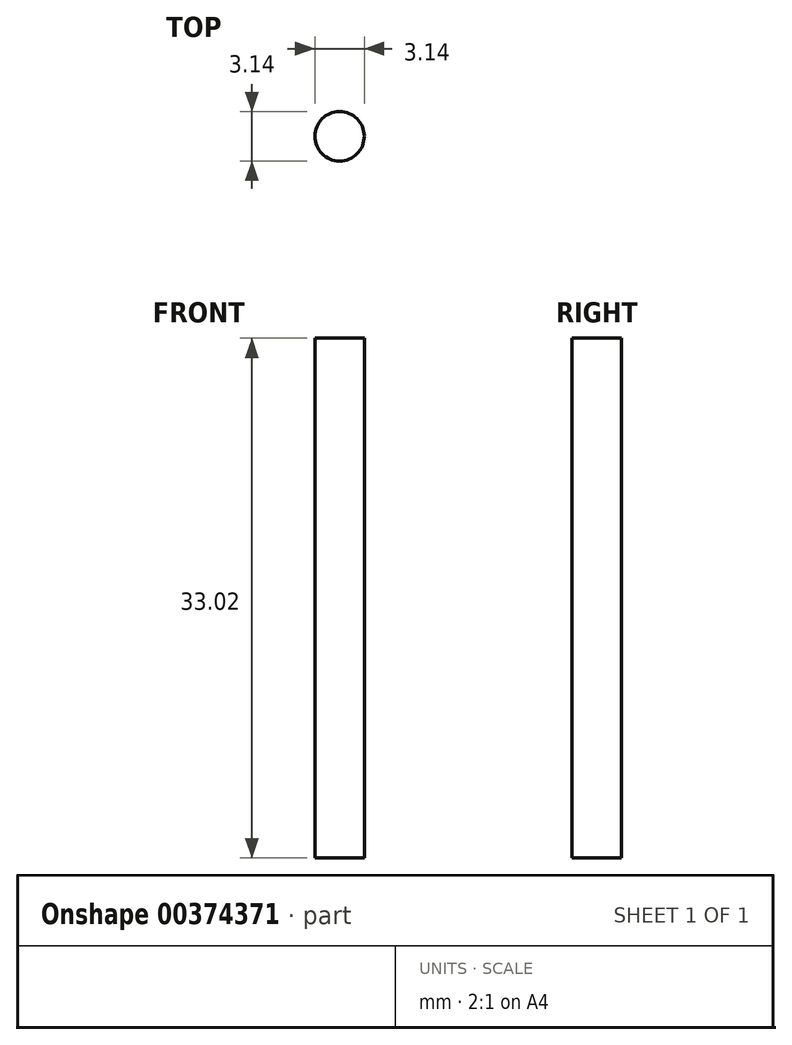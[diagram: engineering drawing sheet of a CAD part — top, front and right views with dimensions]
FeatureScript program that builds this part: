
annotation { "Feature Type Name" : "Feature", "Feature Type Description" : "" }
export const myFeature = defineFeature(function(context is Context, id is Id, definition is map)
    precondition{}
    {
        {
            var Q0;
            Q0=qCreatedBy(makeId("Top.planeOp"),FACE);
            var sketch = newSketch(context, id + "F0", { "sketchPlane" : qUnion([Q0])});
            skCircle(sketch, "E0", {"center": v(0, 0) * mm, "radius": 1.57 * mm});
            skSolve(sketch);
        }
        {
            var Q0;
            Q0=makeQuery(id+"F0.imprint","IMPRINT",FACE,{"disambiguationData":[TD([[makeQuery(id+"F0.imprint","IMPRINT",EDGE,{"derivedFrom":sQuery(id+"F0.wireOp",EDGE,"E0")}),1.0]])]});
            extrude(context, id + "F1", {"entities" : qUnion([Q0]), "oppositeDirection" : true, "depth" : 33.02 * mm});
        }
    });
